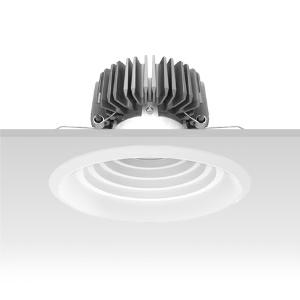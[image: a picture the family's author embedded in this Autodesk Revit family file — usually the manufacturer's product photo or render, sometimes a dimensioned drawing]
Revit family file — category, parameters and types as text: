
# Revit family: 3f_filippi_-_3f_reno_bianco_ugr_3f_filippi_-_30758_-_3f_reno_200_wh_3000-840_dali_ugr
name_source: partatom
category: Lighting Fixtures
units: mm (PartAtom-declared; Revit-internal decimal feet)

## family parameters
Cut with Voids When Loaded = No
Host = Face
Light Source = No
Part Type = Normal
Room Calculation Point = No
Round Connector Dimension = Use Diameter
Shared = No

## types (1)
- 3F Filippi - 3F Reno Bianco UGR (1 x LED, 3300 lm, 28 W, 4000 K)
    Apparent Load = 28 VA
    Approval mark = CE
    CIE Flux Codes = 90 100 100 100 100
    Color Rendering = 80
    Color Temperature = 4000 K
    Control Gear = Electronic transformer
    Default Elevation = 1800 mm
    Description = ILLUMINOTECHNICAL
Luminous efficiency 100% (DLOR 100%, ULOR 0%).
Initial luminous flux of the luminaire 3300 lm.
Direct symmetric UGR distribution.
Installation Interdistance Transv.D = 0.99 x hu - Long.D = 1.01 x hu.
Average luminance <500 cd/m² for radial angles >65°.
Tabular UGR (CIE 117 - 4H-8H; S=0.25H; 70/50/20): RUG 18.4 - 18.3.
Beam angle: 64° - 65°.
Luminous efficacy 118 lm/W.
Lifetime (L90/B10): 30000 h. (tq+25°C)
Lifetime (L85/B10): 50000 h. (tq+25°C)
Lifetime (L70/B10): 80000 h. (tq+25°C)
Sudden decreased luminous flux after 50000 hours: 0% (C0).
Photobiological safety in compliance with IEC/TR 62778: RG1 low risk, (IEC 62471).
In compliance with IEC/EN 62722-2-1 - IEC/EN 62717 standards.

SOURCE
Compact LED module 3000/840.
Energy efficiency class (UE 2019/2020 - UE 2019/2015): E.
CIE 13.3 Colour rendering index: CRI >80 (R9 <50%).
IES TM-30 Fidelity Index: Rf = 84 Rg = 95.
CCT nominal colour temperature 4000 K.
Colour initial tolerance (MacAdam): SDCM 3.
Zhaga Book 3 compliant.

MECHANICAL
Passive heat dissipator in die-casting aluminium, oversized, for optimum thermal management of the LED module.
Parabolic element with graduated/concentric rings in white polycarbonate.
Internal specular metallic louvre to optimise control of the luminous flux in polycarbonate.
Transparent external lens with glossy and satin differentiated surfaces, with a cooling and anti-insect system in methacrylate (PMMA).
Fastening spring clips in stainless steel.
Dimensions: diameter 216 mm, height 142 mm. Weight 1.41 kg.
IP44 protection degree for exposed part, IP20 for recessed part.
Mechanical strength to impacts IK04 (0.5 joule).
Glow-wire test resistance 650°C.

ELECTRICAL
Wiring on a separate unit.
Halogen Free DALI-2 DATI (Parts 251, 252, 253), PUSH-DIM, electronic wiring 230V-50/60Hz, power factor 0.97 at full load, THD <25%, constant output current, SELV, class II, 1 driver, 1 DALI addresse.
Power of the luminaire 28 W.
ENEC - CE.
SAFE FLICKER: PstLM=<1 and SVM=<0.4 (IEC TR 61547-1 and IEC TR 63158), to ensure a more comfortable and safe light.
Luminaire compliant with EN 60598-2-22 for power supply from a centralised emergency system CPSS (Central Power Supply System), not incorporated in the luminaire - high risk areas excluded. The default power and flux are 100% in AC and 100% in DC.
Ambient temperature from 0°C to +25°C.
Temperature class T6 max 85°C.
Relative humidity UR: <85%.

INSTALLATION
Pull-up recessed fitting.
False ceiling carving: 200 mm.
All accessories dedicated to this product are available on the Catalog and on our website www.3F-Filippi.com.

APPLICATIONS
In environments with VDTs, managerial offices and staterooms, public offices and schools.
In false ceilings with narrow voids.

LIGHT MANAGEMENT
Recommended minimum setting: 10%.
The luminaire, equipped with (DALI-2 DATI) driver, can be controlled manually with 3F Easy Dim technology or automatically/manually with wired or wireless DALI/D2D control systems.
The D2D driver guarantees interoperability with other devices with the same certification by making the following information available:
Device Data (Part 251), Energy Report (Part 252), Diagnosis & Maintenance (Part 253).
In electrical systems without a regulation system (manual or automatic) and DALI bus, a suitable jumper must be made on the DA-DA terminals of the appliance.

WARNING
Luminaire designed for disposal/recycling at end-of-life.
Replaceable (LED only) light source by a professional. Replaceable control gear by a professional.
    Height = 0 mm  [stored 0 ft]
    Lamp = 1 x LED
    Lamp Light Flux = 3300 lm
    Lamp Power = 28 W
    Lamp count = 1
    Length = 216 mm
    Lifetime = 50000 h
    Luminous efficacy = 118 lm/W
    Manufacturer = 3F Filippi
    ModVariant = No
    Model = 3F Filippi - 30758 - 3F Reno 200 WH 3000-840 DALI UGR
    Mounting Place = Ceiling
    Mounting Type = Recessed
    Number of Poles = 1
    OnlyDefault = Yes
    Power Factor = 1
    Product Name = 3F Filippi - 3F Reno Bianco UGR
    Product group = recessed luminaire
    ProductGroupID = 4
    Protection Class = Protection class II
    Protection Degree = IP 20
    RLX_Detail_Level = 1
    RLX_Emergency_Light_Flux = 0 lm
    RLX_Emergency_Type = 0
    RLX_Emergency_Type_DB = No
    RlxData = <blob elided: 95197 chars, md5=888600e4>
    Socket = socket
    Standby Power = 0 W
    System Light Flux = 3300 lm
    System Power = 28 W
    Type Comments = Product without accessories
    Type Image = 3ffilippi_3f_reno_200_wh_2500_3000_4000.jpg
    URL = http://relux.com
    VarID = ---
    Voltage = 0 V
    Weight = 0.00 kg
    Width = 0 mm  [stored 0 ft]

note: [stored X ft] marks values corroborated as IEEE doubles in the binary element streams (Revit-internal decimal feet)

## geometry (parser evidence)
native form markers: Blend x4, Sweep x10
no freeform markers — native parametric forms only
